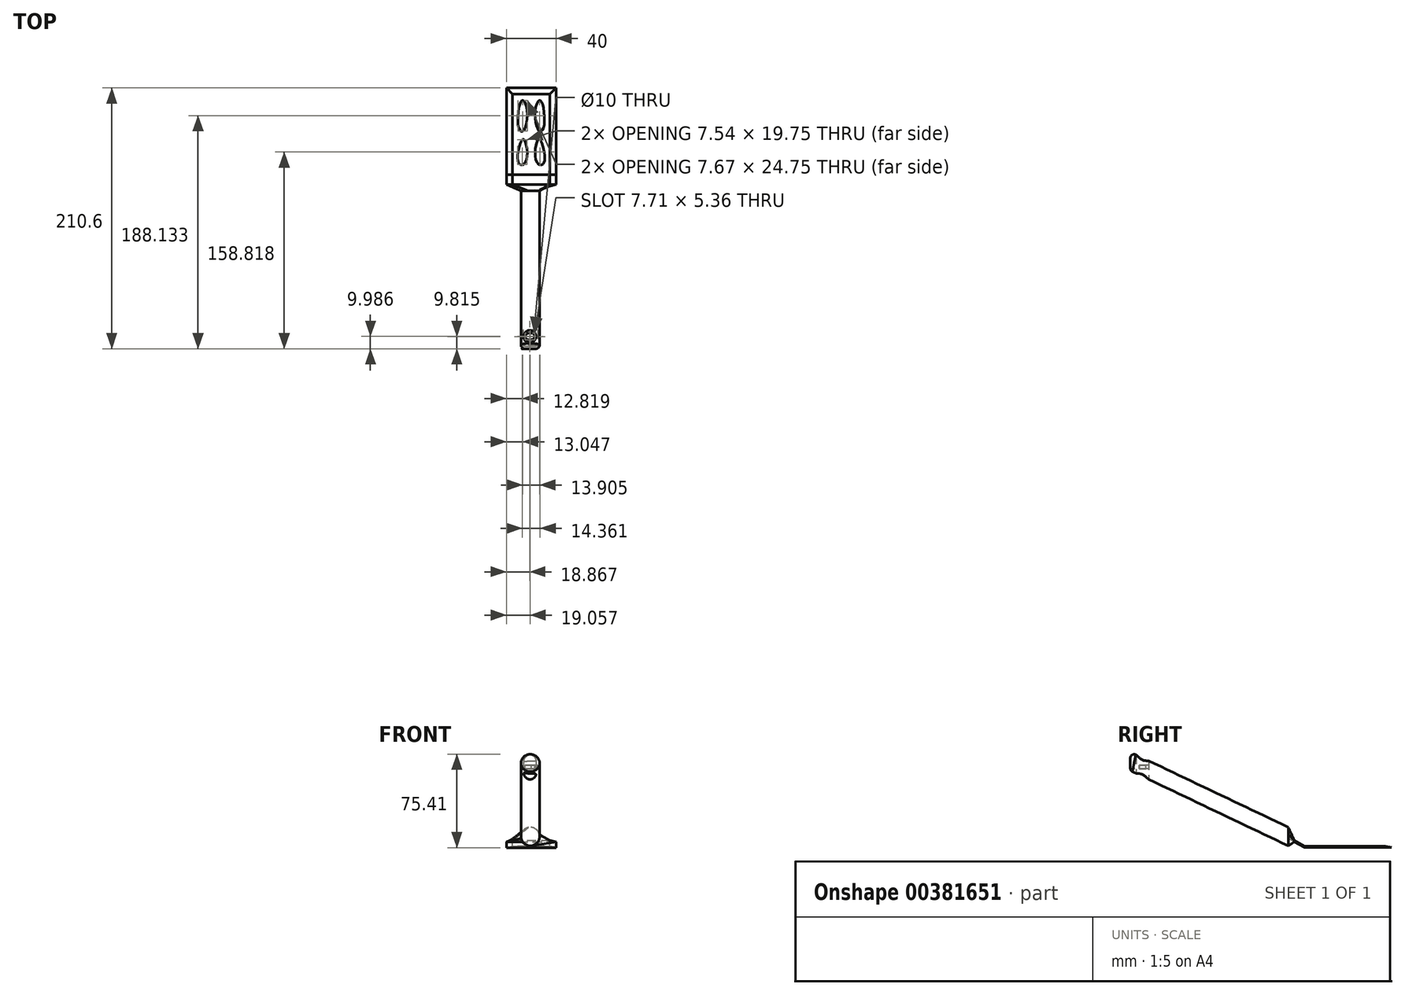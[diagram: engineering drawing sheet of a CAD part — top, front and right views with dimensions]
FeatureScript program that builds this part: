
annotation { "Feature Type Name" : "Feature", "Feature Type Description" : "" }
export const myFeature = defineFeature(function(context is Context, id is Id, definition is map)
    precondition{}
    {
        {
            var Q0;
            Q0=qCreatedBy(makeId("Top.planeOp"),FACE);
            var sketch = newSketch(context, id + "F0", { "sketchPlane" : qUnion([Q0])});
            skLineSegment(sketch, "E0.bottom", {"start": v(-20, 35) * mm, "end": v(20, 35) * mm});
            skLineSegment(sketch, "E0.top", {"start": v(-20, -35) * mm, "end": v(20, -35) * mm});
            skLineSegment(sketch, "E0.left", {"start": v(-20, 35) * mm, "end": v(-20, -35) * mm});
            skLineSegment(sketch, "E0.right", {"start": v(20, 35) * mm, "end": v(20, -35) * mm});
            skLineSegment(sketch, "E1", {"start": v(-50.62, -35) * mm, "end": v(46, -35) * mm, "construction": true});
            skPoint(sketch, "E1.endSnap0", {"position": v(0, -35) * mm});
            skSolve(sketch);
        }
        {
            var Q0;
            Q0=qCreatedBy(makeId("Top.planeOp"),FACE);
            cPlane(context, id + "F1", {"entities" : qUnion([Q0]), "cplaneType" : CPlaneType.OFFSET, "offset" : 1 * mm, "width" : 150 * mm, "height" : 150 * mm});
        }
        {
            var Q0;
            Q0=qCreatedBy(id+"F1.planeOp",FACE);
            var sketch = newSketch(context, id + "F2", { "sketchPlane" : qUnion([Q0])});
            skLineSegment(sketch, "E2.bottom", {"start": v(-15, 30) * mm, "end": v(15, 30) * mm});
            skLineSegment(sketch, "E2.top", {"start": v(-15, -35) * mm, "end": v(15, -35) * mm});
            skLineSegment(sketch, "E2.left", {"start": v(-15, 30) * mm, "end": v(-15, -35) * mm});
            skLineSegment(sketch, "E2.right", {"start": v(15, 30) * mm, "end": v(15, -35) * mm});
            skLineSegment(sketch, "E3", {"start": v(-47.68, -35) * mm, "end": v(42.74, -35) * mm, "construction": true});
            skSolve(sketch);
        }
        {
            var Q0;
            Q0=makeQuery(id+"F0.imprint","IMPRINT",FACE,{"disambiguationData":[TD([[makeQuery(id+"F0.imprint","IMPRINT",EDGE,{"derivedFrom":sQuery(id+"F0.wireOp",EDGE,"E0.bottom")}),-1.0]])]});
            var Q1;
            Q1=makeQuery(id+"F2.imprint","IMPRINT",FACE,{"disambiguationData":[TD([[makeQuery(id+"F2.imprint","IMPRINT",EDGE,{"derivedFrom":sQuery(id+"F2.wireOp",EDGE,"E2.bottom")}),-1.0]])]});
            loft(context, id + "F3", {"sheetProfilesArray" : [{ "sheetProfileEntities" : qUnion([Q0]) }, { "sheetProfileEntities" : qUnion([Q1]) }]});
        }
        {
            var Q0;
            Q0=makeQuery(id+"F3.opLoft","SWEPT_FACE",FACE,{"disambiguationData":[OSD([sQuery(id+"F0.wireOp",EDGE,"E0.top"),sQuery(id+"F0.wireOp",EDGE,"E0.left"),sQuery(id+"F0.wireOp",EDGE,"E0.right"),sQuery(id+"F2.wireOp",EDGE,"E2.top"),sQuery(id+"F2.wireOp",EDGE,"E2.left"),sQuery(id+"F2.wireOp",EDGE,"E2.right")])]});
            var sketch = newSketch(context, id + "F4", { "sketchPlane" : qUnion([Q0])});
            skLineSegment(sketch, "E4", {"start": v(-20, 0) * mm, "end": v(20, 0) * mm});
            skLineSegment(sketch, "E5", {"start": v(20, 0) * mm, "end": v(15, 1) * mm});
            skLineSegment(sketch, "E6", {"start": v(15, 1) * mm, "end": v(-15, 1) * mm});
            skLineSegment(sketch, "E7", {"start": v(-15, 1) * mm, "end": v(-20, 0) * mm});
            skSolve(sketch);
        }
        {
            var Q0;
            Q0=qCreatedBy(makeId("Right.planeOp"),FACE);
            var sketch = newSketch(context, id + "F5", { "sketchPlane" : qUnion([Q0])});
            skLineSegment(sketch, "E8", {"start": v(-34.84, 0) * mm, "end": v(-43.14, 4.75) * mm});
            skSolve(sketch);
        }
        {
            var Q0;
            Q0=makeQuery(id+"F4.imprint","IMPRINT",FACE,{"disambiguationData":[TD([[makeQuery(id+"F4.imprint","IMPRINT",EDGE,{"derivedFrom":sQuery(id+"F4.wireOp",EDGE,"E4")}),1.0]])]});
            var Q1;
            Q1=sQuery(id+"F5.wireOp",EDGE,"E8");
            sweep(context, id + "F6", {"operationType" : NewBodyOperationType.ADD, "profiles" : qUnion([Q0]), "path" : qUnion([Q1])});
        }
        {
            var Q0;
            Q0=makeQuery(id+"F6.opSweep","CAP_FACE",FACE,{"disambiguationData":[OSD([sQuery(id+"F4.wireOp",EDGE,"E4"),sQuery(id+"F4.wireOp",EDGE,"E5"),sQuery(id+"F4.wireOp",EDGE,"E6"),sQuery(id+"F4.wireOp",EDGE,"E7"),sQuery(id+"F5.wireOp",VERTEX,"E8.end")])],"isStart":false});
            cPlane(context, id + "F7", {"entities" : qUnion([Q0]), "cplaneType" : CPlaneType.OFFSET, "offset" : 5 * mm, "width" : 150 * mm, "height" : 150 * mm});
        }
        {
            var Q0;
            Q0=qCreatedBy(id+"F7.planeOp",FACE);
            var sketch = newSketch(context, id + "F8", { "sketchPlane" : qUnion([Q0])});
            skCircle(sketch, "E9", {"center": v(-0.7, 8.85) * mm, "radius": 7.5 * mm});
            skSolve(sketch);
        }
        {
            var Q1;
            Q1=makeQuery(id+"F6.opSweep","CAP_FACE",FACE,{"disambiguationData":[OSD([sQuery(id+"F4.wireOp",EDGE,"E4"),sQuery(id+"F4.wireOp",EDGE,"E5"),sQuery(id+"F4.wireOp",EDGE,"E6"),sQuery(id+"F4.wireOp",EDGE,"E7"),sQuery(id+"F5.wireOp",VERTEX,"E8.end")])],"isStart":false});
            var Q2;
            Q2=makeQuery(id+"F8.imprint","IMPRINT",FACE,{"disambiguationData":[TD([[makeQuery(id+"F8.imprint","IMPRINT",EDGE,{"derivedFrom":sQuery(id+"F8.wireOp",EDGE,"E9")}),1.0]])]});
            loft(context, id + "F9", {"operationType" : NewBodyOperationType.ADD, "sheetProfilesArray" : [{ "sheetProfileEntities" : qUnion([Q1]) }, { "sheetProfileEntities" : qUnion([Q2]) }]});
        }
        {
            var Q0;
            Q0=makeQuery(id+"F3.opLoft","CAP_FACE",FACE,{"disambiguationData":[OSD([makeQuery(id+"F2.imprint","IMPRINT",FACE,{"disambiguationData":[TD([[makeQuery(id+"F2.imprint","IMPRINT",EDGE,{"derivedFrom":sQuery(id+"F2.wireOp",EDGE,"E2.bottom")}),-1.0]])]})])],"isStart":true});
            var sketch = newSketch(context, id + "F10", { "sketchPlane" : qUnion([Q0])});
            skFitSpline(sketch, "E10", {"points": [v(-7.4, 24.9) * mm, v(-10.3, 3.83) * mm, v(-6.78, 0) * mm, v(-3.26, 16.5) * mm, v(-7.4, 24.9) * mm]});
            skLineSegment(sketch, "E11", {"start": v(0, 0) * mm, "end": v(0, 30) * mm, "construction": true});
            skLineSegment(sketch, "E12", {"start": v(0, 30) * mm, "end": v(0, -35) * mm, "construction": true});
            skFitSpline(sketch, "E13", {"points": [v(-10.05, -14.5) * mm, v(-9.42, -26.6) * mm, v(-4.18, -24.33) * mm, v(-5.9, -6.53) * mm, v(-10.05, -14.5) * mm]});
            skFitSpline(sketch, "E14.MirrorC", {"points": [v(7.4, 24.9) * mm, v(10.3, 3.83) * mm, v(6.78, 0) * mm, v(3.26, 16.5) * mm, v(7.4, 24.9) * mm]});
            skFitSpline(sketch, "E15.MirrorC", {"points": [v(10.05, -14.5) * mm, v(9.42, -26.6) * mm, v(4.18, -24.33) * mm, v(5.9, -6.53) * mm, v(10.05, -14.5) * mm]});
            skSolve(sketch);
        }
        {
            var Q0;
            Q0=makeQuery(id+"F10.imprint","IMPRINT",FACE,{"disambiguationData":[TD([[makeQuery(id+"F10.imprint","IMPRINT",EDGE,{"derivedFrom":sQuery(id+"F10.wireOp",EDGE,"E10")}),1.0]])]});
            var Q1;
            Q1=makeQuery(id+"F10.imprint","IMPRINT",FACE,{"disambiguationData":[TD([[makeQuery(id+"F10.imprint","IMPRINT",EDGE,{"derivedFrom":sQuery(id+"F10.wireOp",EDGE,"E14.MirrorC")}),-1.0]])]});
            var Q2;
            Q2=makeQuery(id+"F10.imprint","IMPRINT",FACE,{"disambiguationData":[TD([[makeQuery(id+"F10.imprint","IMPRINT",EDGE,{"derivedFrom":sQuery(id+"F10.wireOp",EDGE,"E13")}),1.0]])]});
            var Q3;
            Q3=makeQuery(id+"F10.imprint","IMPRINT",FACE,{"disambiguationData":[TD([[makeQuery(id+"F10.imprint","IMPRINT",EDGE,{"derivedFrom":sQuery(id+"F10.wireOp",EDGE,"E15.MirrorC")}),-1.0]])]});
            extrude(context, id + "F11", {"entities" : qUnion([Q0, Q1, Q2, Q3]), "operationType" : NewBodyOperationType.REMOVE, "oppositeDirection" : true, "depth" : 25 * mm});
        }
        {
            var Q0;
            Q0=qCreatedBy(makeId("Right.planeOp"),FACE);
            var sketch = newSketch(context, id + "F12", { "sketchPlane" : qUnion([Q0])});
            skLineSegment(sketch, "E16", {"start": v(-48.36, 8.7) * mm, "end": v(-175.82, 69.41) * mm});
            skSolve(sketch);
        }
        {
            var Q0;
            Q0=makeQuery(id+"F9.opLoft","CAP_FACE",FACE,{"disambiguationData":[OSD([makeQuery(id+"F8.imprint","IMPRINT",FACE,{"disambiguationData":[TD([[makeQuery(id+"F8.imprint","IMPRINT",EDGE,{"derivedFrom":sQuery(id+"F8.wireOp",EDGE,"E9")}),1.0]])]})])],"isStart":true});
            var Q1;
            Q1=sQuery(id+"F12.wireOp",EDGE,"E16");
            sweep(context, id + "F13", {"profiles" : qUnion([Q0]), "path" : qUnion([Q1])});
        }
        {
            var Q0;
            Q0=makeQuery(id+"F13.opSweep","CAP_FACE",FACE,{"disambiguationData":[OSD([makeQuery(id+"F8.imprint","IMPRINT",FACE,{"disambiguationData":[TD([[makeQuery(id+"F8.imprint","IMPRINT",EDGE,{"derivedFrom":sQuery(id+"F8.wireOp",EDGE,"E9")}),1.0]])]}),sQuery(id+"F12.wireOp",VERTEX,"E16.end")])],"isStart":false});
            fillet(context, id + "F14", {"entities" : qUnion([Q0]), "radius" : 3 * mm, "tangentPropagation" : true, "allowEdgeOverflow" : false});
        }
        {
            var Q0;
            Q0=qCreatedBy(makeId("Top.planeOp"),FACE);
            var sketch = newSketch(context, id + "F15", { "sketchPlane" : qUnion([Q0])});
            skCircle(sketch, "E17", {"center": v(-1.13, -165.79) * mm, "radius": 5 * mm});
            skSolve(sketch);
        }
        {
            var Q0;
            Q0 = qSketchRegion(id + "F15", true);
            extrude(context, id + "F16", {"entities" : qUnion([Q0]), "operationType" : NewBodyOperationType.REMOVE, "depth" : 144 * mm});
        }
        {
            var Q0;
            Q0=makeQuery(id+"F13.opSweep","CAP_FACE",FACE,{"disambiguationData":[OSD([makeQuery(id+"F8.imprint","IMPRINT",FACE,{"disambiguationData":[TD([[makeQuery(id+"F8.imprint","IMPRINT",EDGE,{"derivedFrom":sQuery(id+"F8.wireOp",EDGE,"E9")}),1.0]])]}),sQuery(id+"F12.wireOp",VERTEX,"E16.end")])],"isStart":false});
            cPlane(context, id + "F17", {"entities" : qUnion([Q0]), "cplaneType" : CPlaneType.OFFSET, "offset" : 3 * mm, "oppositeDirection" : true, "width" : 150 * mm, "height" : 150 * mm});
        }
        {
            var Q0;
            Q0=qCreatedBy(id+"F17.planeOp",FACE);
            var sketch = newSketch(context, id + "F18", { "sketchPlane" : qUnion([Q0])});
            skLineSegment(sketch, "E18.bottom", {"start": v(5.24, 66.43) * mm, "end": v(-6.7, 66.43) * mm});
            skLineSegment(sketch, "E18.top", {"start": v(5.24, 63.74) * mm, "end": v(-6.7, 63.74) * mm});
            skLineSegment(sketch, "E18.left", {"start": v(5.24, 63.74) * mm, "end": v(5.24, 66.43) * mm});
            skLineSegment(sketch, "E18.right", {"start": v(-6.7, 63.74) * mm, "end": v(-6.7, 66.43) * mm});
            skSolve(sketch);
        }
        {
            var Q0;
            Q0=makeQuery(id+"F18.imprint","IMPRINT",FACE,{"disambiguationData":[TD([[makeQuery(id+"F18.imprint","IMPRINT",EDGE,{"derivedFrom":sQuery(id+"F18.wireOp",EDGE,"E18.bottom")}),1.0]])]});
            extrude(context, id + "F19", {"entities" : qUnion([Q0]), "oppositeDirection" : true, "depth" : 12.2 * mm});
        }
        {
            var Q0;
            Q0=makeQuery(id+"F19.opExtrude","SWEPT_FACE",FACE,{"disambiguationData":[OSD([sQuery(id+"F18.wireOp",EDGE,"E18.bottom")])]});
            var sketch = newSketch(context, id + "F20", { "sketchPlane" : qUnion([Q0])});
            skArc(sketch, "E19", {"start": v(-2.56, -163.23) * mm, "mid": v(-4.8, -166) * mm, "end": v(-2.06, -168.3) * mm});
            skLineSegment(sketch, "E20", {"start": v(-2.06, -168.3) * mm, "end": v(0, -168.12) * mm});
            skLineSegment(sketch, "E21", {"start": v(-2.56, -163.23) * mm, "end": v(0, -162.94) * mm});
            skArc(sketch, "E22", {"start": v(0, -168.12) * mm, "mid": v(2.91, -165.53) * mm, "end": v(0, -162.94) * mm});
            skSolve(sketch);
        }
        {
            var Q0;
            Q0=makeQuery(id+"F20.imprint","IMPRINT",FACE,{"disambiguationData":[TD([[makeQuery(id+"F20.imprint","IMPRINT",EDGE,{"derivedFrom":sQuery(id+"F20.wireOp",EDGE,"E19")}),1.0]])]});
            extrude(context, id + "F21", {"entities" : qUnion([Q0]), "operationType" : NewBodyOperationType.REMOVE, "oppositeDirection" : true, "depth" : 25 * mm});
        }
    });
